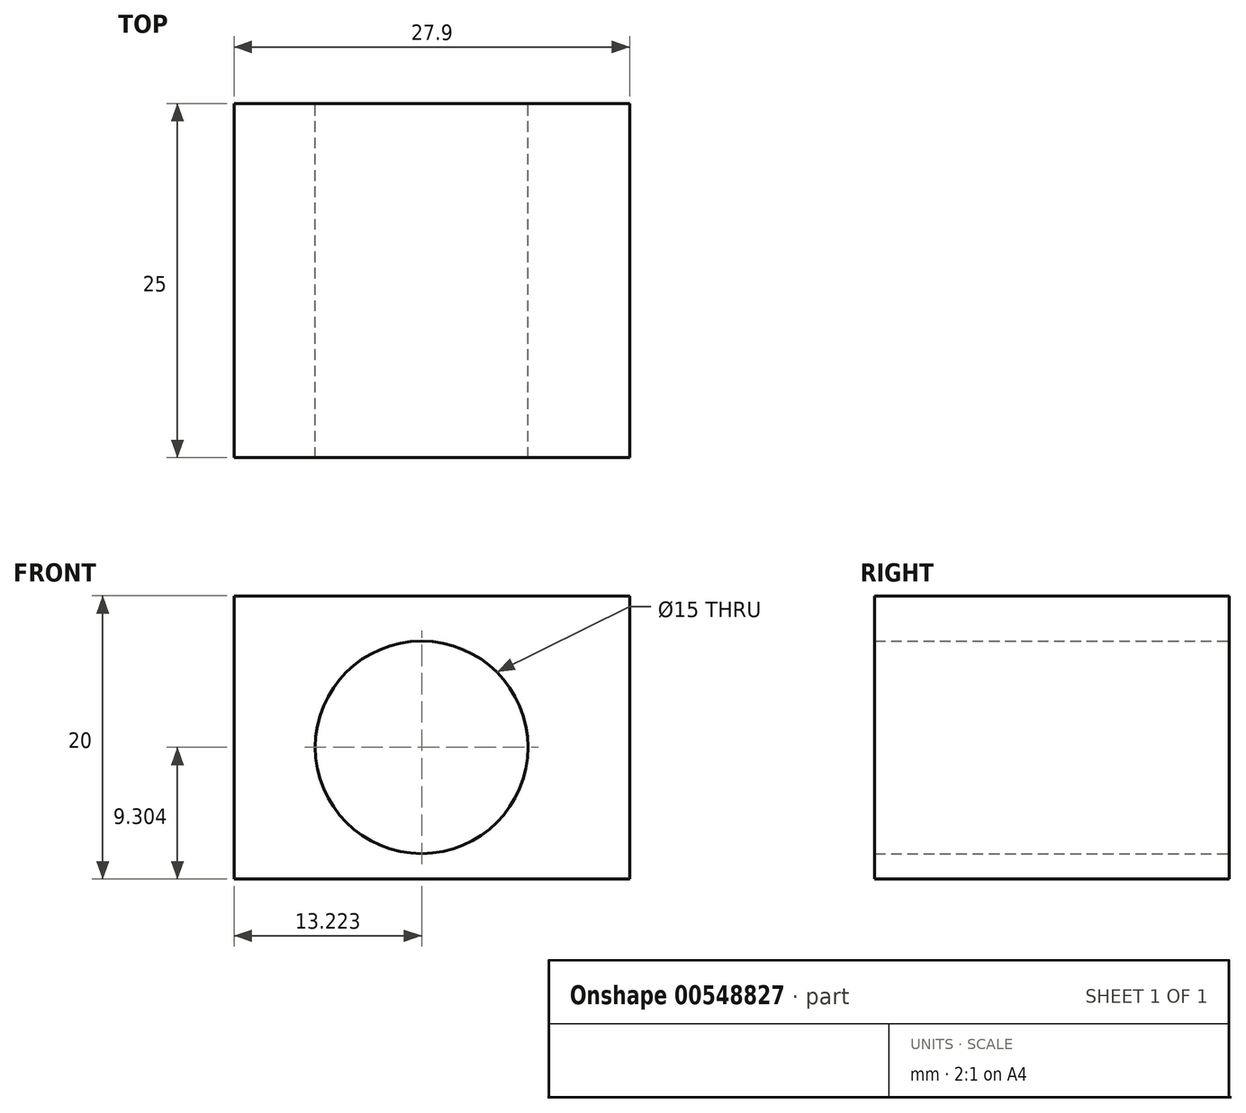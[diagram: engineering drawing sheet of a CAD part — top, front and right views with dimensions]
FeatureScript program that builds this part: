
annotation { "Feature Type Name" : "Feature", "Feature Type Description" : "" }
export const myFeature = defineFeature(function(context is Context, id is Id, definition is map)
    precondition{}
    {
        {
            var Q0;
            Q0=qCreatedBy(makeId("Front.planeOp"),FACE);
            var sketch = newSketch(context, id + "F0", { "sketchPlane" : qUnion([Q0])});
            skLineSegment(sketch, "E0.bottom", {"start": v(-11.6, 5.92) * mm, "end": v(16.31, 5.92) * mm});
            skLineSegment(sketch, "E0.top", {"start": v(-11.6, -14.08) * mm, "end": v(16.31, -14.08) * mm});
            skLineSegment(sketch, "E0.left", {"start": v(-11.6, 5.92) * mm, "end": v(-11.6, -14.08) * mm});
            skLineSegment(sketch, "E0.right", {"start": v(16.31, 5.92) * mm, "end": v(16.31, -14.08) * mm});
            skCircle(sketch, "E1", {"center": v(1.63, -4.78) * mm, "radius": 7.5 * mm});
            skSolve(sketch);
        }
        {
            var Q0;
            Q0 = qSketchRegion(id + "F0", true);
            extrude(context, id + "F1", {"entities" : qUnion([Q0]), "depth" : 25 * mm, "offsetDistance" : 25 * mm});
        }
    });
